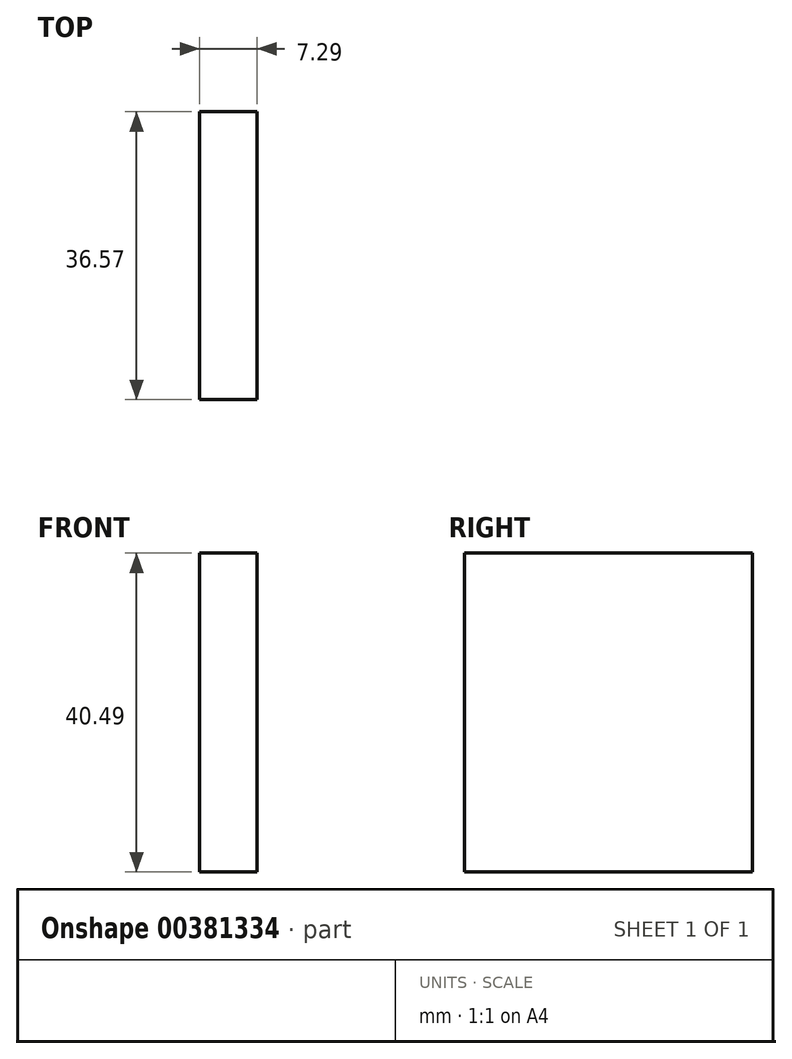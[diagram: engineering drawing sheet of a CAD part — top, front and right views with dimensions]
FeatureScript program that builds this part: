
annotation { "Feature Type Name" : "Feature", "Feature Type Description" : "" }
export const myFeature = defineFeature(function(context is Context, id is Id, definition is map)
    precondition{}
    {
        {
            var Q0;
            Q0=qCreatedBy(makeId("Right.planeOp"),FACE);
            var sketch = newSketch(context, id + "F0", { "sketchPlane" : qUnion([Q0])});
            skLineSegment(sketch, "E0", {"start": v(47.38, 0) * mm, "end": v(47.38, -40.5) * mm});
            skLineSegment(sketch, "E1", {"start": v(47.38, -40.5) * mm, "end": v(10.81, -40.5) * mm});
            skLineSegment(sketch, "E2", {"start": v(10.81, -40.5) * mm, "end": v(10.81, 0) * mm});
            skLineSegment(sketch, "E3", {"start": v(10.81, 0) * mm, "end": v(47.38, 0) * mm});
            skSolve(sketch);
        }
        {
            var Q0;
            Q0=makeQuery(id+"F0.imprint","IMPRINT",FACE,{"disambiguationData":[TD([[makeQuery(id+"F0.imprint","IMPRINT",EDGE,{"derivedFrom":sQuery(id+"F0.wireOp",EDGE,"E0")}),-1.0]])]});
            extrude(context, id + "F1", {"entities" : qUnion([Q0]), "oppositeDirection" : true, "depth" : 7.3 * mm});
        }
    });
